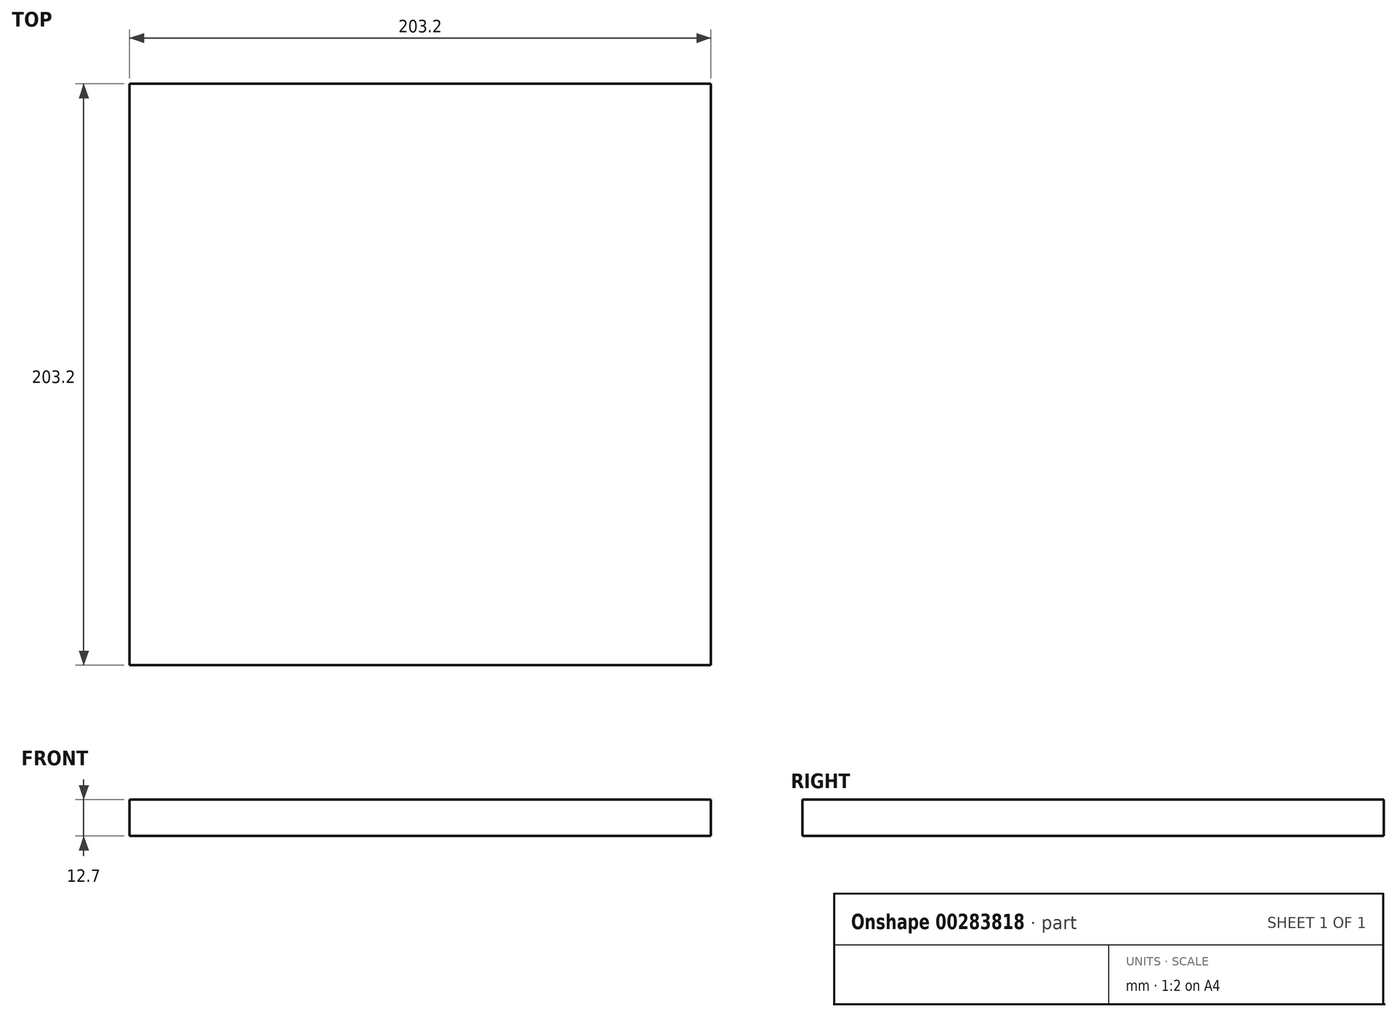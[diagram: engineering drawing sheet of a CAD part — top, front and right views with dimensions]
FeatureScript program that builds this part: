
annotation { "Feature Type Name" : "Feature", "Feature Type Description" : "" }
export const myFeature = defineFeature(function(context is Context, id is Id, definition is map)
    precondition{}
    {
        {
            var Q0;
            Q0=qCreatedBy(makeId("Top.planeOp"),FACE);
            var sketch = newSketch(context, id + "F0", { "sketchPlane" : qUnion([Q0])});
            skLineSegment(sketch, "E0.bottom", {"start": v(0, 0) * mm, "end": v(203.2, 0) * mm});
            skLineSegment(sketch, "E0.top", {"start": v(0, 203.2) * mm, "end": v(203.2, 203.2) * mm});
            skLineSegment(sketch, "E0.left", {"start": v(0, 0) * mm, "end": v(0, 203.2) * mm});
            skLineSegment(sketch, "E0.right", {"start": v(203.2, 0) * mm, "end": v(203.2, 203.2) * mm});
            skSolve(sketch);
        }
        {
            var Q0;
            Q0 = qSketchRegion(id + "F0", true);
            extrude(context, id + "F1", {"entities" : qUnion([Q0]), "depth" : 12.7 * mm});
        }
    });
